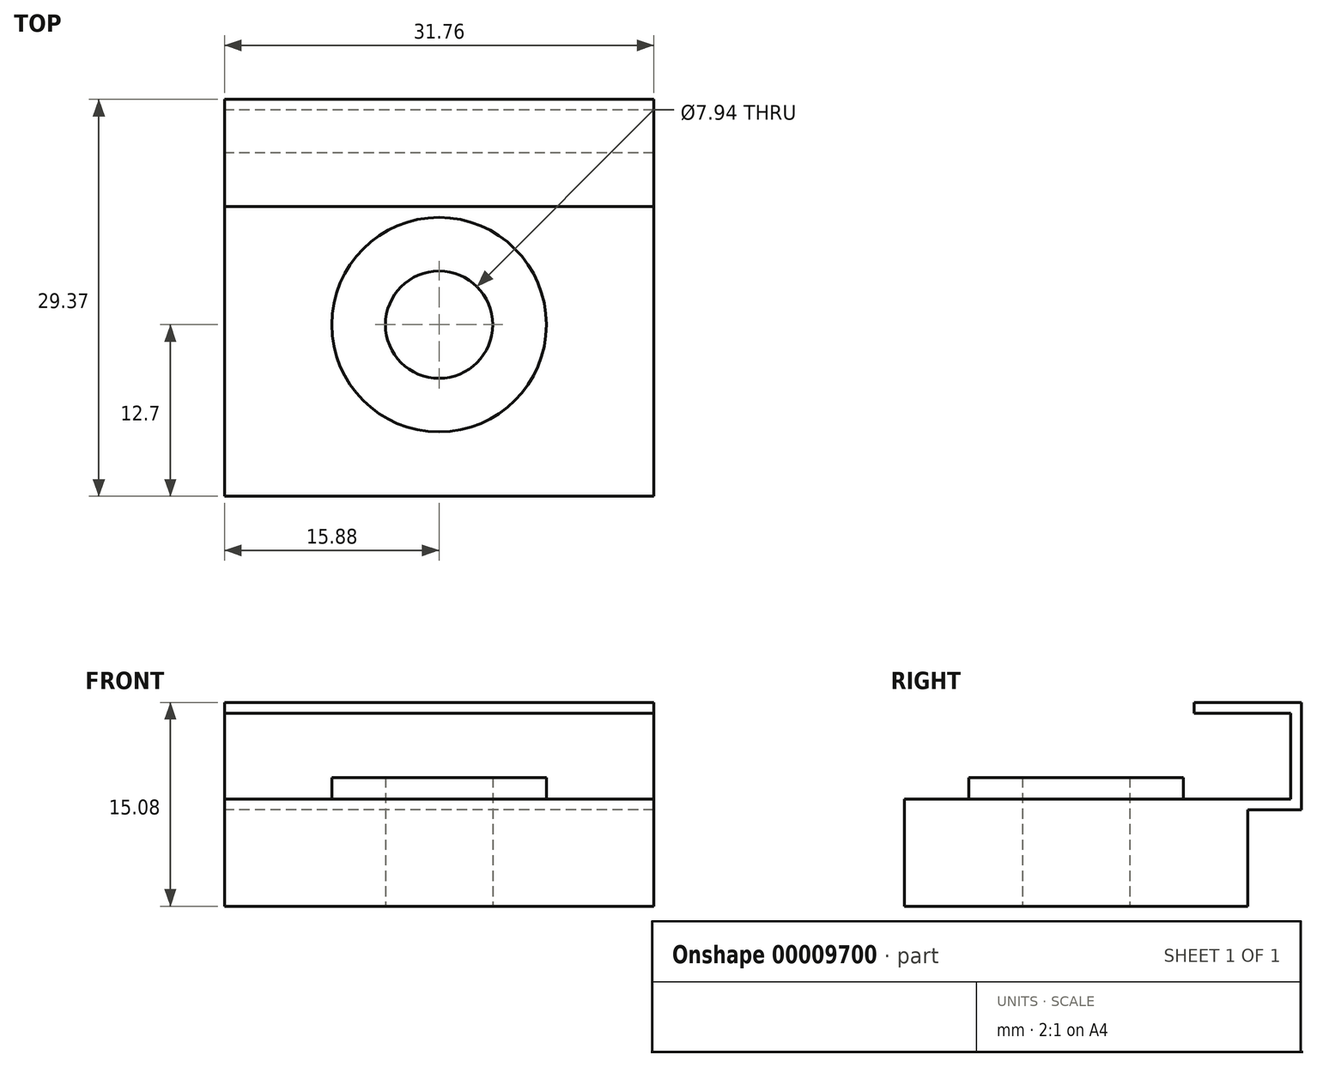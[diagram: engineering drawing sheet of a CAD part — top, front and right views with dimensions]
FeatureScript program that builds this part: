
annotation { "Feature Type Name" : "Feature", "Feature Type Description" : "" }
export const myFeature = defineFeature(function(context is Context, id is Id, definition is map)
    precondition{}
    {
        {
            var Q0;
            Q0=qCreatedBy(makeId("Top.planeOp"),FACE);
            var sketch = newSketch(context, id + "F0", { "sketchPlane" : qUnion([Q0])});
            skLineSegment(sketch, "E0.rect.bottom", {"start": v(15.88, 12.7) * mm, "end": v(-15.88, 12.7) * mm});
            skLineSegment(sketch, "E0.rect.top", {"start": v(15.88, -12.7) * mm, "end": v(-15.88, -12.7) * mm});
            skLineSegment(sketch, "E0.rect.left", {"start": v(15.88, 12.7) * mm, "end": v(15.88, -12.7) * mm});
            skLineSegment(sketch, "E0.rect.right", {"start": v(-15.88, 12.7) * mm, "end": v(-15.88, -12.7) * mm});
            skPoint(sketch, "E0.rect.middle", {"position": v(0, 0) * mm});
            skCircle(sketch, "E1", {"center": v(0, 0) * mm, "radius": 3.97 * mm});
            skSolve(sketch);
        }
        {
            var Q0;
            Q0=makeQuery(id+"F0.imprint","IMPRINT",FACE,{"disambiguationData":[TD([[makeQuery(id+"F0.imprint","IMPRINT",EDGE,{"derivedFrom":sQuery(id+"F0.wireOp",EDGE,"E0.rect.bottom")}),1.0]])]});
            extrude(context, id + "F1", {"entities" : qUnion([Q0]), "depth" : 7.94 * mm});
        }
        {
            var Q0;
            Q0=makeQuery(id+"F1.opExtrude","CAP_FACE",FACE,{"disambiguationData":[OSD([sQuery(id+"F0.wireOp",EDGE,"E0.rect.bottom"),sQuery(id+"F0.wireOp",EDGE,"E0.rect.top"),sQuery(id+"F0.wireOp",EDGE,"E0.rect.left"),sQuery(id+"F0.wireOp",EDGE,"E0.rect.right"),sQuery(id+"F0.wireOp",EDGE,"E1")])],"isStart":false});
            var sketch = newSketch(context, id + "F2", { "sketchPlane" : qUnion([Q0])});
            skCircle(sketch, "E2", {"center": v(0, 0) * mm, "radius": 7.94 * mm});
            skSolve(sketch);
        }
        {
            var Q0;
            Q0=makeQuery(id+"F2.imprint","IMPRINT",FACE,{"disambiguationData":[TD([[makeQuery(id+"F2.imprint","IMPRINT",EDGE,{"derivedFrom":sQuery(id+"F2.wireOp",EDGE,"E2")}),1.0]])]});
            extrude(context, id + "F3", {"entities" : qUnion([Q0]), "operationType" : NewBodyOperationType.ADD, "depth" : 1.59 * mm});
        }
        {
            var Q0;
            Q0=makeQuery(id+"F1.opExtrude","SWEPT_FACE",FACE,{"disambiguationData":[OSD([sQuery(id+"F0.wireOp",EDGE,"E0.rect.right")])]});
            var sketch = newSketch(context, id + "F4", { "sketchPlane" : qUnion([Q0])});
            skLineSegment(sketch, "E3", {"start": v(-12.7, 7.94) * mm, "end": v(-15.87, 7.94) * mm});
            skLineSegment(sketch, "E4", {"start": v(-15.87, 7.94) * mm, "end": v(-15.87, 14.29) * mm});
            skLineSegment(sketch, "E5", {"start": v(-15.87, 14.29) * mm, "end": v(-8.73, 14.29) * mm});
            skLineSegment(sketch, "E6", {"start": v(-8.73, 14.29) * mm, "end": v(-8.73, 15.08) * mm});
            skLineSegment(sketch, "E7", {"start": v(-8.73, 15.08) * mm, "end": v(-16.67, 15.08) * mm});
            skLineSegment(sketch, "E8", {"start": v(-16.67, 15.08) * mm, "end": v(-16.67, 7.14) * mm});
            skLineSegment(sketch, "E9", {"start": v(-16.67, 7.14) * mm, "end": v(-12.7, 7.14) * mm});
            skLineSegment(sketch, "E10", {"start": v(-12.7, 7.14) * mm, "end": v(-12.7, 7.94) * mm});
            skLineSegment(sketch, "E11", {"start": v(-16.67, 11.11) * mm, "end": v(-15.87, 11.11) * mm, "construction": true});
            skSolve(sketch);
        }
        {
            var Q0;
            Q0 = qSketchRegion(id + "F4", true);
            var Q1;
            Q1=makeQuery(id+"F1.opExtrude","SWEPT_FACE",FACE,{"disambiguationData":[OSD([sQuery(id+"F0.wireOp",EDGE,"E0.rect.left")])]});
            extrude(context, id + "F5", {"entities" : qUnion([Q0]), "operationType" : NewBodyOperationType.ADD, "endBound" : BoundingType.UP_TO_SURFACE, "oppositeDirection" : true, "endBoundEntityFace" : qUnion([Q1]), "depth" : 25.4 * mm});
        }
    });
